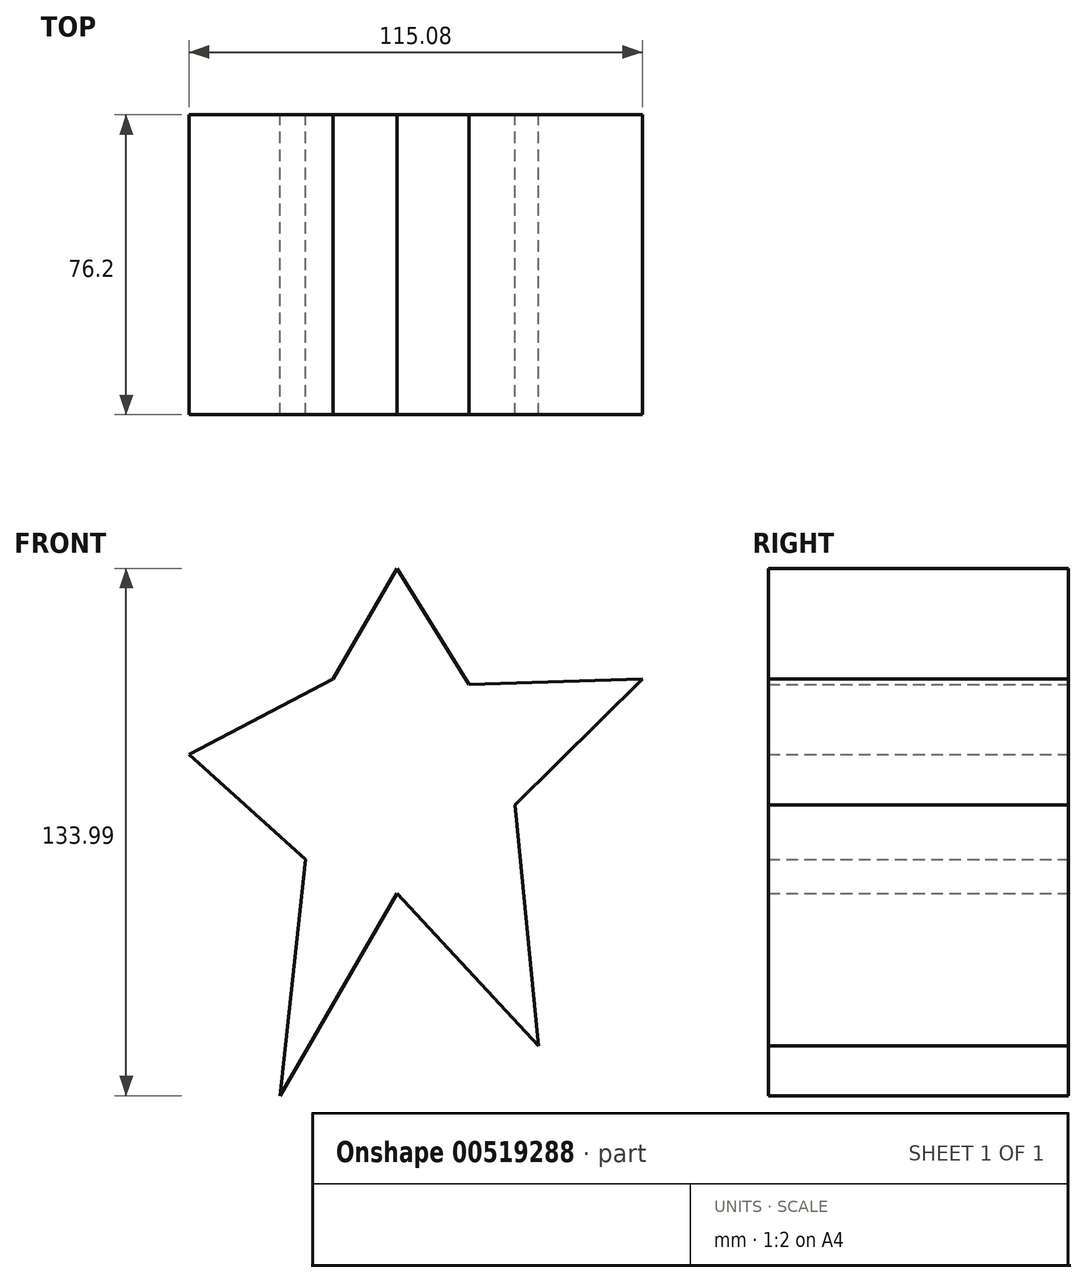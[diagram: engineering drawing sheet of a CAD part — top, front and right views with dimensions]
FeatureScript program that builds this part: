
annotation { "Feature Type Name" : "Feature", "Feature Type Description" : "" }
export const myFeature = defineFeature(function(context is Context, id is Id, definition is map)
    precondition{}
    {
        {
            var Q0;
            Q0=qCreatedBy(makeId("Front.planeOp"),FACE);
            var sketch = newSketch(context, id + "F0", { "sketchPlane" : qUnion([Q0])});
            skLineSegment(sketch, "E0", {"start": v(0, 54.03) * mm, "end": v(-16.24, 25.91) * mm});
            skLineSegment(sketch, "E1", {"start": v(-16.24, 25.91) * mm, "end": v(-52.81, 6.72) * mm});
            skLineSegment(sketch, "E2", {"start": v(-52.81, 6.72) * mm, "end": v(-23.24, -19.88) * mm});
            skLineSegment(sketch, "E3", {"start": v(-23.24, -19.88) * mm, "end": v(-29.7, -79.96) * mm});
            skLineSegment(sketch, "E4", {"start": v(-29.7, -79.96) * mm, "end": v(0, -28.54) * mm});
            skLineSegment(sketch, "E5", {"start": v(0, -28.54) * mm, "end": v(35.87, -67.31) * mm});
            skLineSegment(sketch, "E6", {"start": v(35.87, -67.31) * mm, "end": v(29.96, -6.12) * mm});
            skLineSegment(sketch, "E7", {"start": v(29.96, -6.12) * mm, "end": v(62.27, 25.91) * mm});
            skLineSegment(sketch, "E8", {"start": v(62.27, 25.91) * mm, "end": v(18.3, 24.5) * mm});
            skLineSegment(sketch, "E9", {"start": v(18.3, 24.5) * mm, "end": v(0, 54.03) * mm});
            skSolve(sketch);
        }
        {
            var Q0;
            Q0=makeQuery(id+"F0.imprint","IMPRINT",FACE,{"disambiguationData":[TD([[makeQuery(id+"F0.imprint","IMPRINT",EDGE,{"derivedFrom":sQuery(id+"F0.wireOp",EDGE,"E0")}),1.0]])]});
            extrude(context, id + "F1", {"entities" : qUnion([Q0]), "depth" : 76.2 * mm, "offsetDistance" : 25.4 * mm});
        }
    });
